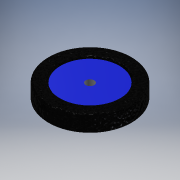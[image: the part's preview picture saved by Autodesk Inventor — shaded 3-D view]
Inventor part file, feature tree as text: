
AUTODESK INVENTOR PART (.ipt)
format: ipt  version: 2017 (Build 210142000, 142)  size: 223,232 bytes
history: native  units: mm
features: revolve x1, sketch x1
ambient origin geometry x8: Origin, YZ Plane, XZ Plane, XY Plane, X Axis, Y Axis, Z Axis, Center Point
bodies: Solid1 (feature_tree)
feature tree (2):
  revolve  "Revolution1"  [1 undecoded]
  sketch  "Sketch1"  dims[d0=560.317934mm d1=40.0mm d2=30.0mm d3=30.0mm d4=200.0mm d5=2.0mm d6=5.0mm d7=20.0mm d8=90.0deg]
note: 1 required parameter value undecoded (feature->parameter linkage not recoverable at this tier; creation-order binding heuristic only, values carry confidence <= 0.55)
